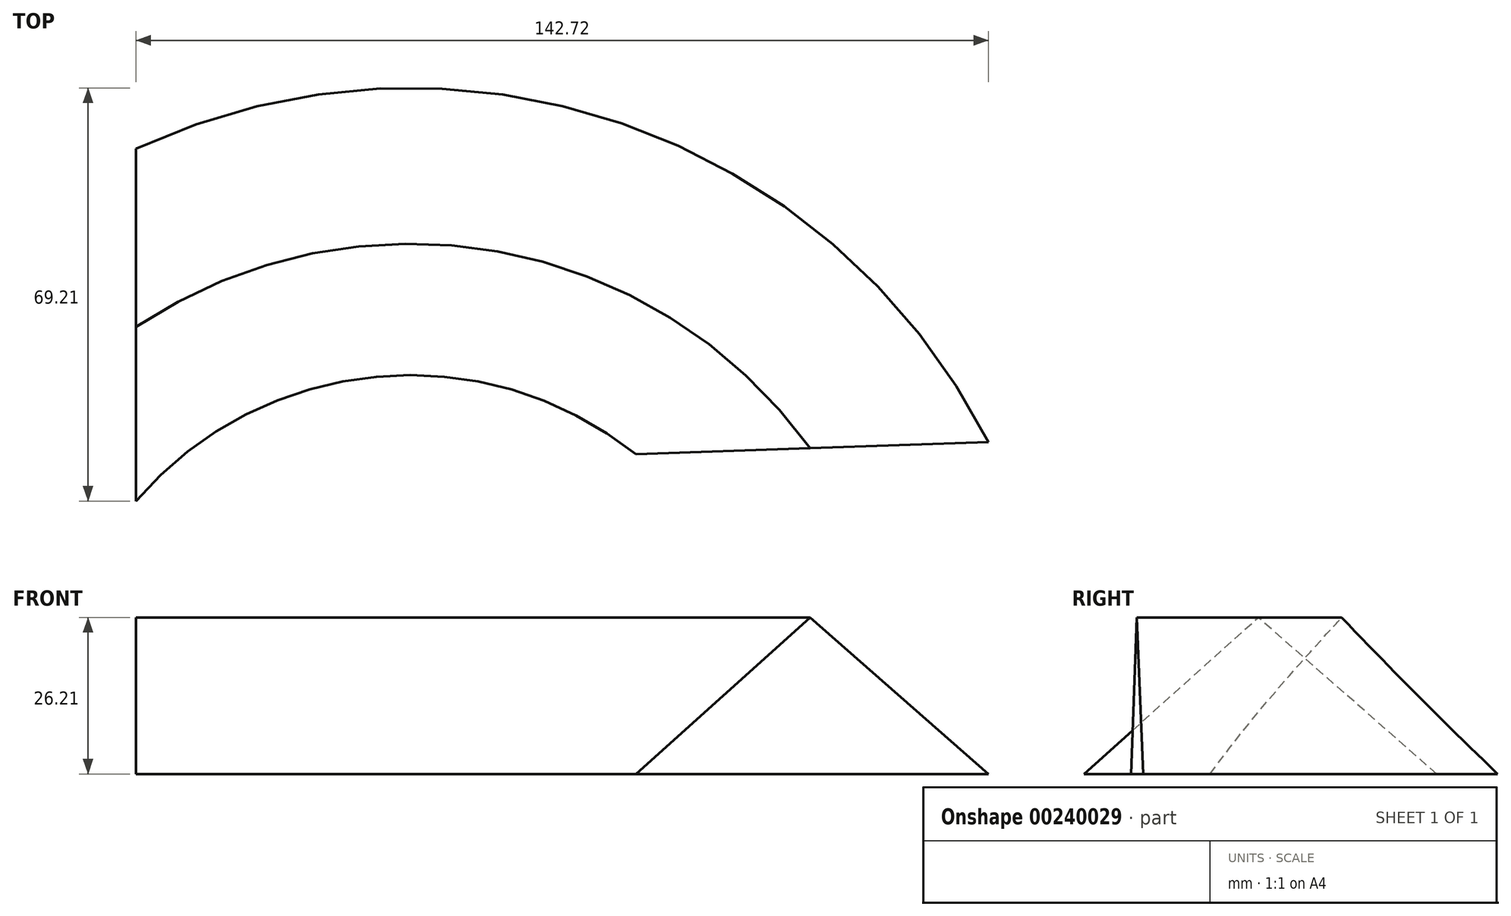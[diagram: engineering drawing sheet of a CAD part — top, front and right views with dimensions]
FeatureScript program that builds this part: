
annotation { "Feature Type Name" : "Feature", "Feature Type Description" : "" }
export const myFeature = defineFeature(function(context is Context, id is Id, definition is map)
    precondition{}
    {
        {
            var Q0;
            Q0=qCreatedBy(makeId("Right.planeOp"),FACE);
            var sketch = newSketch(context, id + "F0", { "sketchPlane" : qUnion([Q0])});
            skLineSegment(sketch, "E0", {"start": v(29.86, 0) * mm, "end": v(-29.17, 0) * mm});
            skLineSegment(sketch, "E1", {"start": v(29.86, 0) * mm, "end": v(0, 26.2) * mm});
            skLineSegment(sketch, "E2", {"start": v(-29.17, 0) * mm, "end": v(0, 26.2) * mm});
            skSolve(sketch);
        }
        {
            var Q0;
            Q0=qCreatedBy(makeId("Top.planeOp"),FACE);
            var sketch = newSketch(context, id + "F1", { "sketchPlane" : qUnion([Q0])});
            skArc(sketch, "E3", {"start": v(112.88, -20.32) * mm, "mid": v(60.55, 12.65) * mm, "end": v(0, 0) * mm});
            skSolve(sketch);
        }
        {
            var Q0;
            Q0=makeQuery(id+"F0.imprint","IMPRINT",FACE,{"disambiguationData":[TD([[makeQuery(id+"F0.imprint","IMPRINT",EDGE,{"derivedFrom":sQuery(id+"F0.wireOp",EDGE,"E0")}),-1.0]])]});
            var Q1;
            Q1=sQuery(id+"F1.wireOp",EDGE,"E3");
            sweep(context, id + "F2", {"profiles" : qUnion([Q0]), "path" : qUnion([Q1])});
        }
    });
